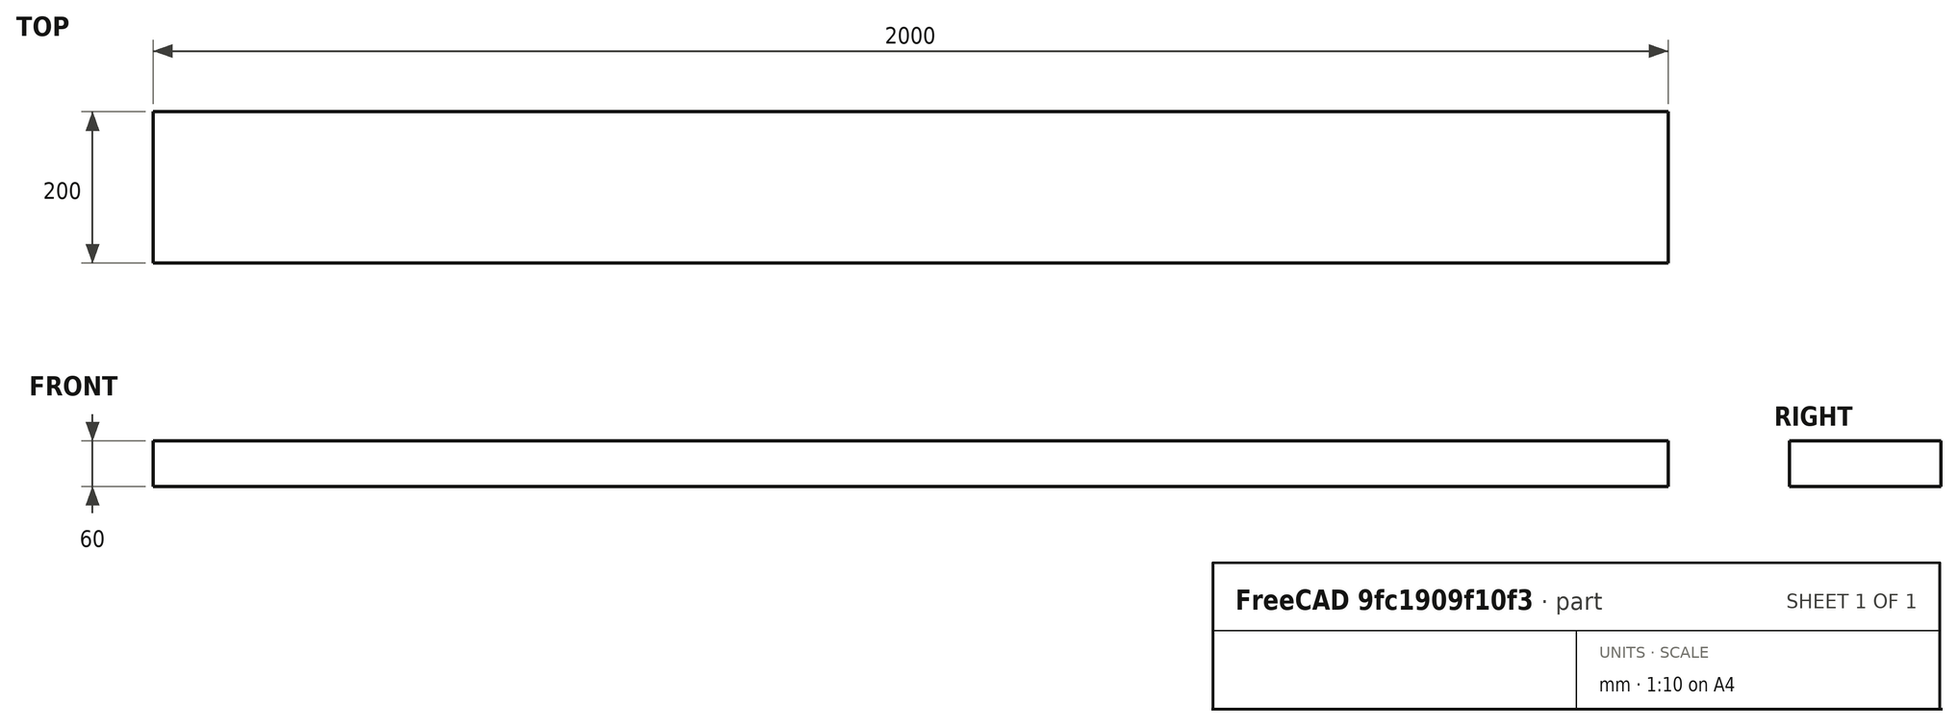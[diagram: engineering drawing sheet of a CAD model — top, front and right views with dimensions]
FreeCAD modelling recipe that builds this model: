
FCSTD DOCUMENT  (FreeCAD 0.18.4R)
Label: Bar
License: All rights reserved
LicenseURL: http://en.wikipedia.org/wiki/All_rights_reserved
objects: Sketcher::SketchObject×1, PartDesign::Pad×1, PartDesign::Body×1, App::Part×1
note: 4 computed .brp shape members not serialized (recipe doc carries the construction recipe); baked Part::Feature solids carry a one-line shape summary decoded from their .brp

FEATURE [Sketcher::SketchObject] Sketch
  MapMode = 5
  Support = -> [XY_Plane001]
  sketch-geometry (4):
    g0: LineSegment StartX=-2.84e-14 StartY=0 StartZ=0 EndX=2000 EndY=0 EndZ=0
    g1: LineSegment StartX=-2.84e-14 StartY=0 StartZ=0 EndX=-2.84e-14 EndY=200 EndZ=0
    g2: LineSegment StartX=-2.84e-14 StartY=200 StartZ=0 EndX=2000 EndY=200 EndZ=0
    g3: LineSegment StartX=2000 StartY=200 StartZ=0 EndX=2000 EndY=0 EndZ=0
  constraints (12):
    c: Horizontal(g0)
    c: Vertical(g1)
    c: Horizontal(g2)
    c: Vertical(g3)
    c: DistanceX(g0,g0) = 2000
    c: DistanceY(g1,g1) = 200
    c: Coincident(g1,g0)
    c: Equal(g2,g0)
    c: Equal(g3,g1)
    c: Coincident(g1,g2)
    c: Coincident(g3,g0)
    c: Coincident(g0,g-1)
FEATURE [PartDesign::Pad] Pad
  Length = 60
  Length2 = 100
  Profile = -> Sketch
  Type = 0
FEATURE [PartDesign::Body] Body
  Group = -> [Sketch,Pad]
  Origin = -> Origin001
  Tip = -> Pad
FEATURE [App::Part] Part
  Group = -> [Body]
  Origin = -> Origin
